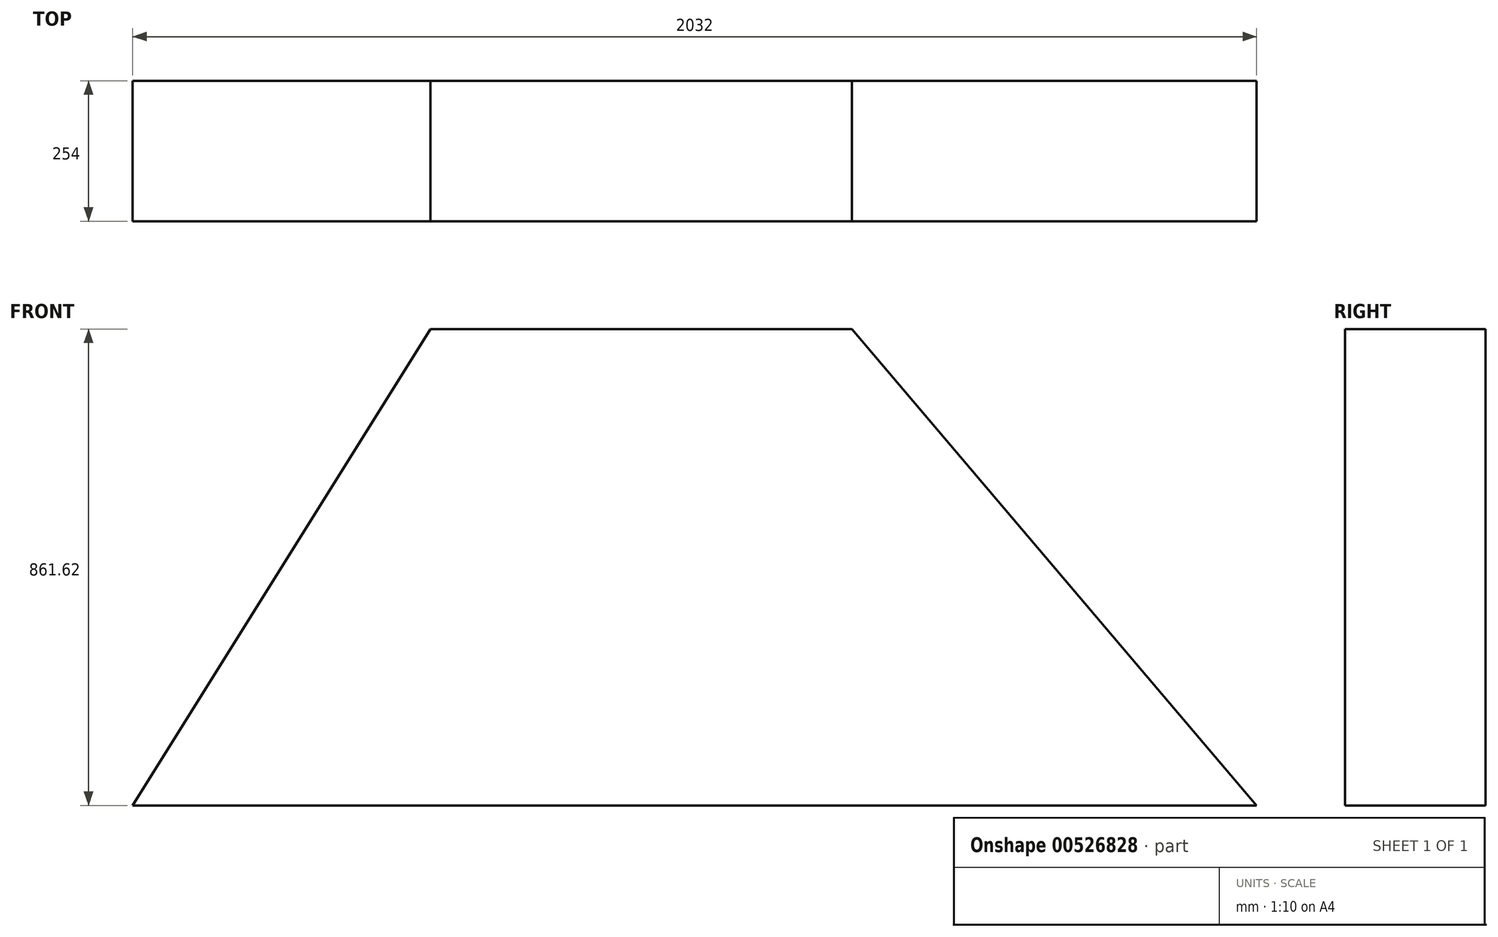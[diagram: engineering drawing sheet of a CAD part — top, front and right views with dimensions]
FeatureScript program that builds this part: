
annotation { "Feature Type Name" : "Feature", "Feature Type Description" : "" }
export const myFeature = defineFeature(function(context is Context, id is Id, definition is map)
    precondition{}
    {
        {
            var Q0;
            Q0=qCreatedBy(makeId("Front.planeOp"),FACE);
            var sketch = newSketch(context, id + "F0", { "sketchPlane" : qUnion([Q0])});
            skLineSegment(sketch, "E0", {"start": v(0, 0) * mm, "end": v(762, 0) * mm});
            skLineSegment(sketch, "E1", {"start": v(0, 0) * mm, "end": v(-538.4, -861.62) * mm});
            skLineSegment(sketch, "E2", {"start": v(-538.4, -861.62) * mm, "end": v(1493.6, -861.62) * mm});
            skLineSegment(sketch, "E3", {"start": v(1493.6, -861.62) * mm, "end": v(762, 0) * mm});
            skSolve(sketch);
        }
        {
            var Q0;
            Q0=makeQuery(id+"F0.imprint","IMPRINT",FACE,{"disambiguationData":[TD([[makeQuery(id+"F0.imprint","IMPRINT",EDGE,{"derivedFrom":sQuery(id+"F0.wireOp",EDGE,"E0")}),-1.0]])]});
            var Q1;
            Q1=makeQuery(id+"F0.imprint","IMPRINT",FACE,{"disambiguationData":[TD([[makeQuery(id+"F0.imprint","IMPRINT",EDGE,{"derivedFrom":sQuery(id+"F0.wireOp",EDGE,"E0")}),-1.0]])]});
            extrude(context, id + "F1", {"entities" : qUnion([Q0, Q1]), "depth" : 254 * mm, "offsetDistance" : 25.4 * mm});
        }
    });
